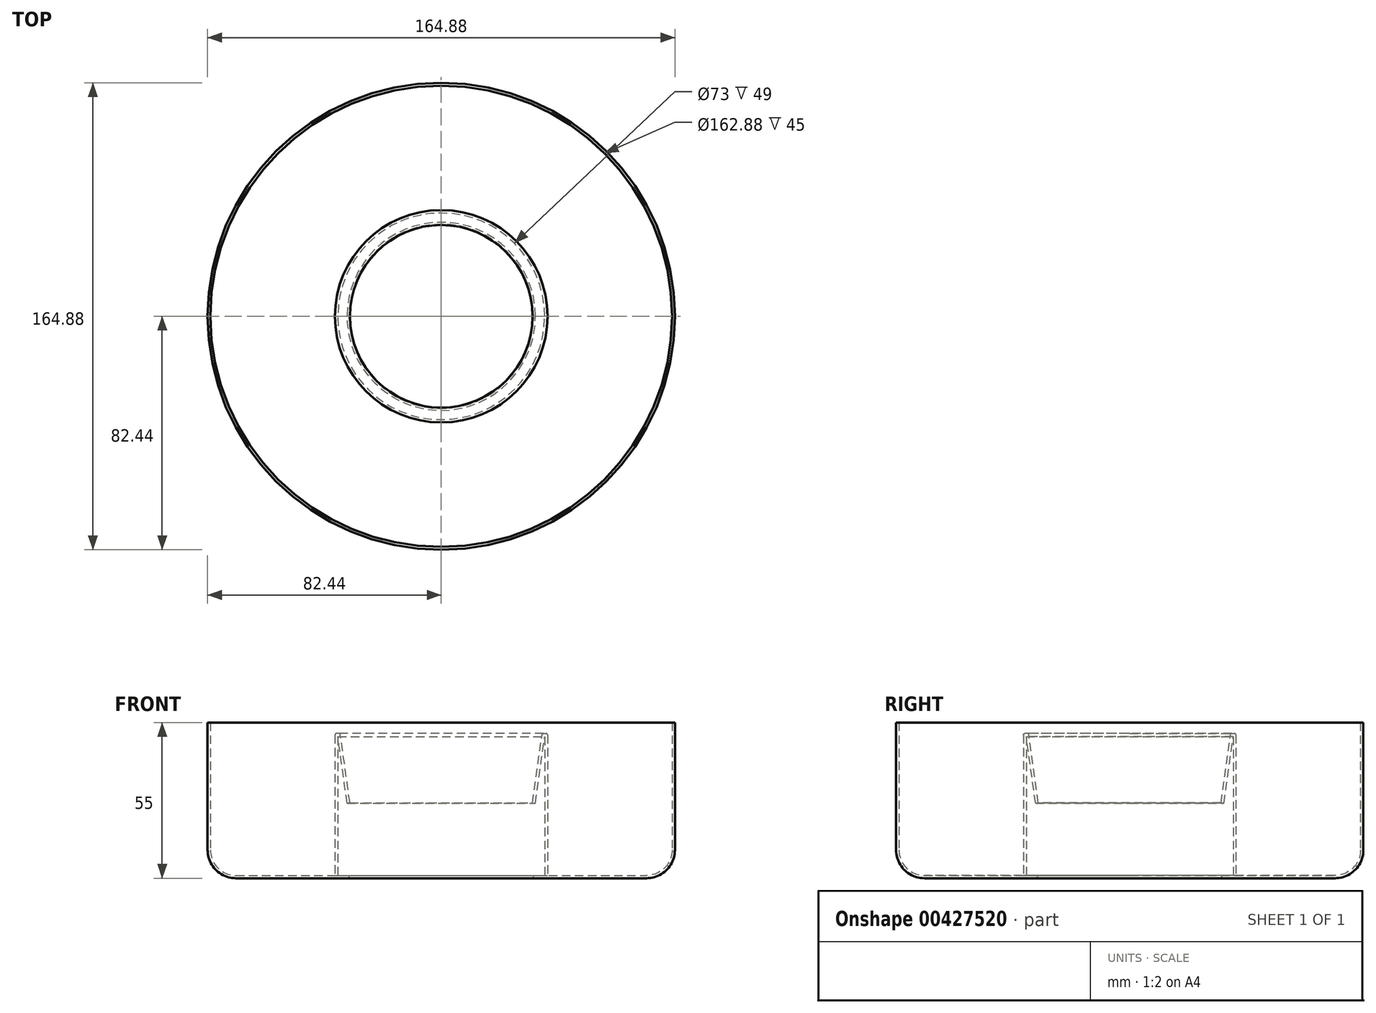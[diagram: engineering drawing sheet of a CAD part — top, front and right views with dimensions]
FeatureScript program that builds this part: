
annotation { "Feature Type Name" : "Feature", "Feature Type Description" : "" }
export const myFeature = defineFeature(function(context is Context, id is Id, definition is map)
    precondition{}
    {
        {
            var Q0;
            Q0=qCreatedBy(makeId("Front.planeOp"),FACE);
            var sketch = newSketch(context, id + "F0", { "sketchPlane" : qUnion([Q0])});
            skLineSegment(sketch, "E0", {"start": v(0, 59.24) * mm, "end": v(0, 9.24) * mm});
            skLineSegment(sketch, "E1", {"start": v(-32.52, 10.24) * mm, "end": v(-32.44, 9.24) * mm});
            skLineSegment(sketch, "E2", {"start": v(0, 9.24) * mm, "end": v(0, 59.24) * mm});
            skLineSegment(sketch, "E3", {"start": v(-32.44, 9.24) * mm, "end": v(-72.44, 9.24) * mm});
            skLineSegment(sketch, "E4", {"start": v(-82.44, 19.24) * mm, "end": v(-82.44, 64.24) * mm});
            skLineSegment(sketch, "E5", {"start": v(-82.44, 64.24) * mm, "end": v(-82.44, 19.24) * mm});
            skPoint(sketch, "E6.visualSharp", {"position": v(-82.44, 9.24) * mm});
            skArc(sketch, "E6.filletArc", {"start": v(-82.44, 19.24) * mm, "mid": v(-79.51, 12.17) * mm, "end": v(-72.44, 9.24) * mm});
            skLineSegment(sketch, "E7.0", {"start": v(-32.44, 10.24) * mm, "end": v(-36.5, 10.24) * mm});
            skArc(sketch, "E7.1", {"start": v(-81.44, 19.24) * mm, "mid": v(-78.8, 12.88) * mm, "end": v(-72.44, 10.24) * mm});
            skLineSegment(sketch, "E7.2", {"start": v(-81.44, 64.24) * mm, "end": v(-81.44, 19.24) * mm});
            skLineSegment(sketch, "E8", {"start": v(-82.44, 64.24) * mm, "end": v(-81.44, 64.24) * mm});
            skLineSegment(sketch, "E9", {"start": v(-36.5, 59.24) * mm, "end": v(-36.5, 10.24) * mm});
            skLineSegment(sketch, "E10", {"start": v(-36.5, 10.24) * mm, "end": v(-36.5, 59.24) * mm});
            skLineSegment(sketch, "E11", {"start": v(-36.5, 59.24) * mm, "end": v(-33.22, 35.72) * mm});
            skLineSegment(sketch, "E12", {"start": v(-33.22, 35.72) * mm, "end": v(-36.5, 59.24) * mm});
            skLineSegment(sketch, "E13.0", {"start": v(-37.5, 10.24) * mm, "end": v(-37.5, 59.24) * mm});
            skLineSegment(sketch, "E14.0", {"start": v(-32.23, 35.86) * mm, "end": v(-35.5, 59.38) * mm});
            skLineSegment(sketch, "E15", {"start": v(-37.5, 59.24) * mm, "end": v(-37.5, 59.85) * mm});
            skLineSegment(sketch, "E16", {"start": v(-35.5, 59.38) * mm, "end": v(-35.59, 59.95) * mm});
            skLineSegment(sketch, "E17", {"start": v(-36.1, 60.38) * mm, "end": v(-37.02, 60.35) * mm});
            skPoint(sketch, "E18.visualSharp", {"position": v(-37.5, 60.33) * mm});
            skArc(sketch, "E18.filletArc", {"start": v(-37.02, 60.35) * mm, "mid": v(-37.36, 60.2) * mm, "end": v(-37.5, 59.85) * mm});
            skPoint(sketch, "E19.visualSharp", {"position": v(-35.65, 60.4) * mm});
            skArc(sketch, "E19.filletArc", {"start": v(-35.59, 59.95) * mm, "mid": v(-35.76, 60.26) * mm, "end": v(-36.1, 60.38) * mm});
            skLineSegment(sketch, "E20", {"start": v(-33.22, 35.72) * mm, "end": v(-32.23, 35.86) * mm});
            skLineSegment(sketch, "E21.trimOffspring", {"start": v(-37.5, 10.24) * mm, "end": v(-72.44, 10.24) * mm});
            skSolve(sketch);
        }
        {
            var Q0;
            {var subQ2=sQuery(id+"F0.wireOp",EDGE,"E1");Q0=makeQuery(id+"F0.imprint","IMPRINT",FACE,{"disambiguationData":[TD([[makeQuery(id+"F0.imprint","IMPRINT",EDGE,{"derivedFrom":subQ2}),-1.0]])]});}
            var Q1;
            Q1=sQuery(id+"F0.wireOp",EDGE,"E2");
            revolve(context, id + "F1", {"entities" : qUnion([Q0]), "axis" : qUnion([Q1]), "revolveType" : RevolveType.FULL});
        }
    });
